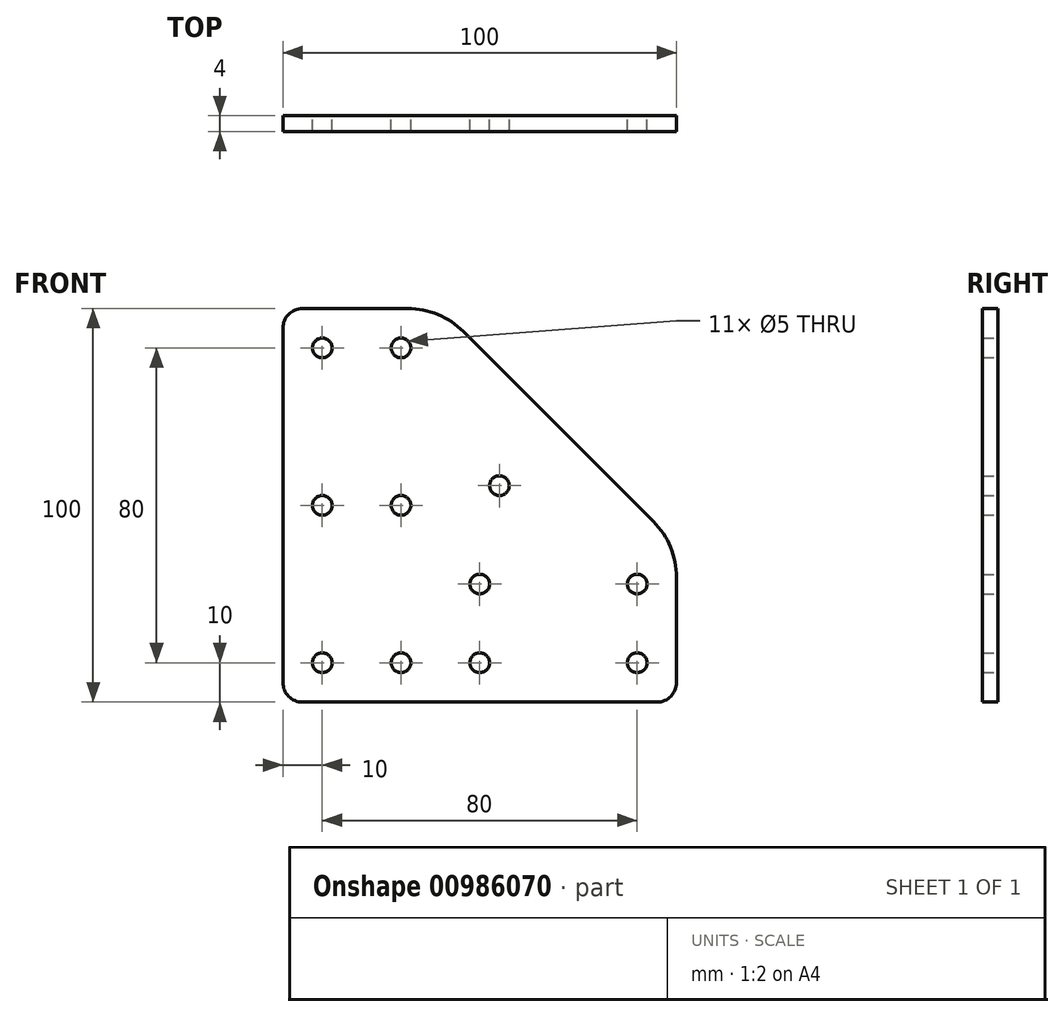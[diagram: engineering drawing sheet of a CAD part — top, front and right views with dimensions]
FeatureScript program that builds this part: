
annotation { "Feature Type Name" : "Feature", "Feature Type Description" : "" }
export const myFeature = defineFeature(function(context is Context, id is Id, definition is map)
    precondition{}
    {
        {
            var Q0;
            Q0=qCreatedBy(makeId("Front.planeOp"),FACE);
            var sketch = newSketch(context, id + "F0", { "sketchPlane" : qUnion([Q0])});
            skLineSegment(sketch, "E0", {"start": v(0, 5) * mm, "end": v(0, 95) * mm});
            skLineSegment(sketch, "E1", {"start": v(5, 100) * mm, "end": v(31.72, 100) * mm});
            skLineSegment(sketch, "E2", {"start": v(45.86, 94.14) * mm, "end": v(94.14, 45.86) * mm});
            skLineSegment(sketch, "E3", {"start": v(100, 31.72) * mm, "end": v(100, 5) * mm});
            skLineSegment(sketch, "E4", {"start": v(95, 0) * mm, "end": v(5, 0) * mm});
            skLineSegment(sketch, "E5", {"start": v(0, 10) * mm, "end": v(100, 10) * mm, "construction": true});
            skLineSegment(sketch, "E6", {"start": v(10, 0) * mm, "end": v(10, 100) * mm, "construction": true});
            skLineSegment(sketch, "E7", {"start": v(30, 100) * mm, "end": v(30, 0) * mm, "construction": true});
            skLineSegment(sketch, "E8", {"start": v(40, 100) * mm, "end": v(40, 0) * mm, "construction": true});
            skLineSegment(sketch, "E9", {"start": v(100, 40) * mm, "end": v(40, 40) * mm, "construction": true});
            skLineSegment(sketch, "E10", {"start": v(40, 40) * mm, "end": v(70, 70) * mm, "construction": true});
            skCircle(sketch, "E11", {"center": v(10, 10) * mm, "radius": 2.5 * mm});
            skCircle(sketch, "E12", {"center": v(30, 10) * mm, "radius": 2.5 * mm});
            skLineSegment(sketch, "E13", {"start": v(0, 90) * mm, "end": v(40, 90) * mm, "construction": true});
            skLineSegment(sketch, "E14", {"start": v(0, 50) * mm, "end": v(40, 50) * mm, "construction": true});
            skCircle(sketch, "E15", {"center": v(10, 90) * mm, "radius": 2.5 * mm});
            skCircle(sketch, "E16", {"center": v(30, 90) * mm, "radius": 2.5 * mm});
            skCircle(sketch, "E17", {"center": v(10, 50) * mm, "radius": 2.5 * mm});
            skCircle(sketch, "E18", {"center": v(30, 50) * mm, "radius": 2.5 * mm});
            skLineSegment(sketch, "E19", {"start": v(90, 0) * mm, "end": v(90, 40) * mm, "construction": true});
            skCircle(sketch, "E20", {"center": v(90, 10) * mm, "radius": 2.5 * mm});
            skCircle(sketch, "E21", {"center": v(55, 55) * mm, "radius": 2.5 * mm});
            skLineSegment(sketch, "E22", {"start": v(50, 0) * mm, "end": v(50, 40) * mm, "construction": true});
            skLineSegment(sketch, "E23", {"start": v(0, 30) * mm, "end": v(100, 30) * mm, "construction": true});
            skCircle(sketch, "E24", {"center": v(50, 10) * mm, "radius": 2.5 * mm});
            skCircle(sketch, "E25", {"center": v(50, 30) * mm, "radius": 2.5 * mm});
            skCircle(sketch, "E26", {"center": v(90, 30) * mm, "radius": 2.5 * mm});
            skPoint(sketch, "E27.visualSharp", {"position": v(40, 100) * mm});
            skArc(sketch, "E27.filletArc", {"start": v(45.86, 94.14) * mm, "mid": v(39.37, 98.48) * mm, "end": v(31.72, 100) * mm});
            skPoint(sketch, "E28.visualSharp", {"position": v(100, 40) * mm});
            skArc(sketch, "E28.filletArc", {"start": v(100, 31.72) * mm, "mid": v(98.48, 39.37) * mm, "end": v(94.14, 45.86) * mm});
            skPoint(sketch, "E29.visualSharp", {"position": v(0, 100) * mm});
            skArc(sketch, "E29.filletArc", {"start": v(5, 100) * mm, "mid": v(1.46, 98.54) * mm, "end": v(0, 95) * mm});
            skPoint(sketch, "E30.visualSharp", {"position": v(0, 0) * mm});
            skArc(sketch, "E30.filletArc", {"start": v(0, 5) * mm, "mid": v(1.46, 1.46) * mm, "end": v(5, 0) * mm});
            skPoint(sketch, "E31.visualSharp", {"position": v(100, 0) * mm});
            skArc(sketch, "E31.filletArc", {"start": v(95, 0) * mm, "mid": v(98.54, 1.46) * mm, "end": v(100, 5) * mm});
            skSolve(sketch);
        }
        {
            var Q0;
            Q0 = qSketchRegion(id + "F0", true);
            extrude(context, id + "F1", {"entities" : qUnion([Q0]), "depth" : 4 * mm, "offsetDistance" : 25 * mm});
        }
    });
